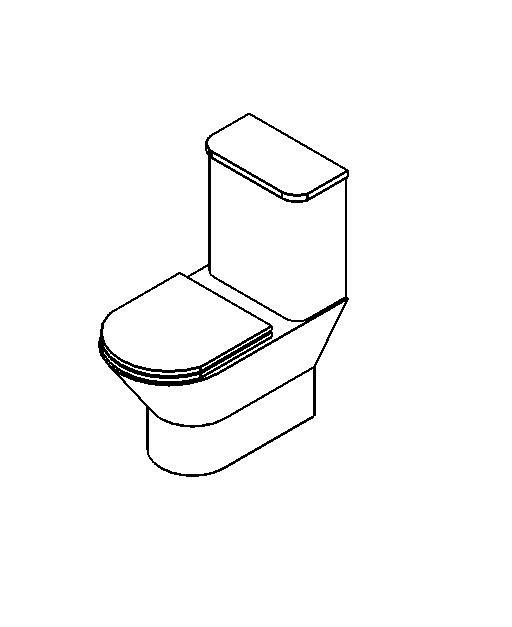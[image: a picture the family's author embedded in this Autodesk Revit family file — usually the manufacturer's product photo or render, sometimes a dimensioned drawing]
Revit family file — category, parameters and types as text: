
# Revit family: Deca_Bacia Sanitaria para Caixa Acoplada_Carrara_P.606
name_source: partatom
category: Plumbing Fixtures
units: mm (PartAtom-declared; Revit-internal decimal feet)

## family parameters
Cut with Voids When Loaded = No
Host = Face
OmniClass Number = 23.45.05.21.11.11
OmniClass Title = Water Operated Water Closets
Part Type = Normal
Room Calculation Point = No
Round Connector Dimension = Use Radius
Shared = No

## types (5) — shared parameters
Acompanha o Produto = -
Aprovado por = quattroD
Atendimento ao Cliente = 0800-0117073
Categoria = BACIAS E BIDES
Composição Anel Vedação = Não Possui
Composição Assento = -
Composição Básica = Argila, feldspato, caulim, vidrados e corantes inorgânicos.
Composição Componente = Não Possui
Consumo = 6 lpf
Cor Interna = -
Cor Secundária = -
Cores Componente = -
Criado por = quattroD
Código Pai = P.606
Description = Bacia para caixa acoplada
Diâmetro Ponto de Esgoto = 0.1 m
Diâmetro Água Fria = 0.02 m
Informações Complementares = -
Itens de Instalação = -
Linha = Carrara
Manufacturer = Deca
Norma = NBR-16727-1;NBR-16727-2
Peso Líquido (Kg) = 36.572
Pressão máx. funcionamento = -
Pressão mín. Aquec. Acúmulo = -
Pressão mín. Aquec. Passagem = -
Pressão mín. funcionamento = -
Raio Ponto de Esgoto = 0.05 m
Raio Água Fria = 0.01 m
Saída de Esgoto = Saída de Esgoto Vertical
Segmento = Banheiro Luxo
Tipo de dispositivo economizador = -
Tipo de mecanismo utilizado = -
Tipo de rosca de entrada = -
Tipo de rosca de saída = -
URL = www.deca.com.br
Vazão na Pressão máx. (L/min) = -
Vazão na Pressão mín. (L/min) = -
zero-valued in all types: Default Elevation

## per-type parameters (varying)
| type | Combinação | Cor Principal | Material | Model |
| P.606.37_Creme | Deca_Caixa acoplada com acionamento Duo_Cx. Acoplada Univ. Luxo_CD.11F : CD.11F.37_Creme | Creme | Deca_Creme | P.606.37 |
| P.606.22_Marrom Fosco | Deca_Caixa acoplada com acionamento Duo_Cx. Acoplada Univ. Luxo_CD.11F : CD.11F.22_Marrom | Marrom Fosco | Deca_Marrom Fosco | P.606.22 |
| P.606.17_Branco | Deca_Caixa acoplada com acionamento Duo_Cx. Acoplada Univ. Luxo_CD.11F : CD.11F.17_Branco | Branco | Deca_Branco | P.606.17 |
| P.606.94_Ébano Fosco | Deca_Caixa acoplada com acionamento Duo_Cx. Acoplada Univ. Luxo_CD.11F : CD.11F.94_Ébano Fosco | Ébano Fosco | Deca_Ébano Fosco | P.606.94 |
| P.606.95_Ébano | Deca_Caixa acoplada com acionamento Duo_Cx. Acoplada Univ. Luxo_CD.11F : CD.11F.95_Ébano | Ébano | Deca_Ébano | P.606.95 |

## geometry (parser evidence)
native form markers: Sweep x5
no freeform markers — native parametric forms only
